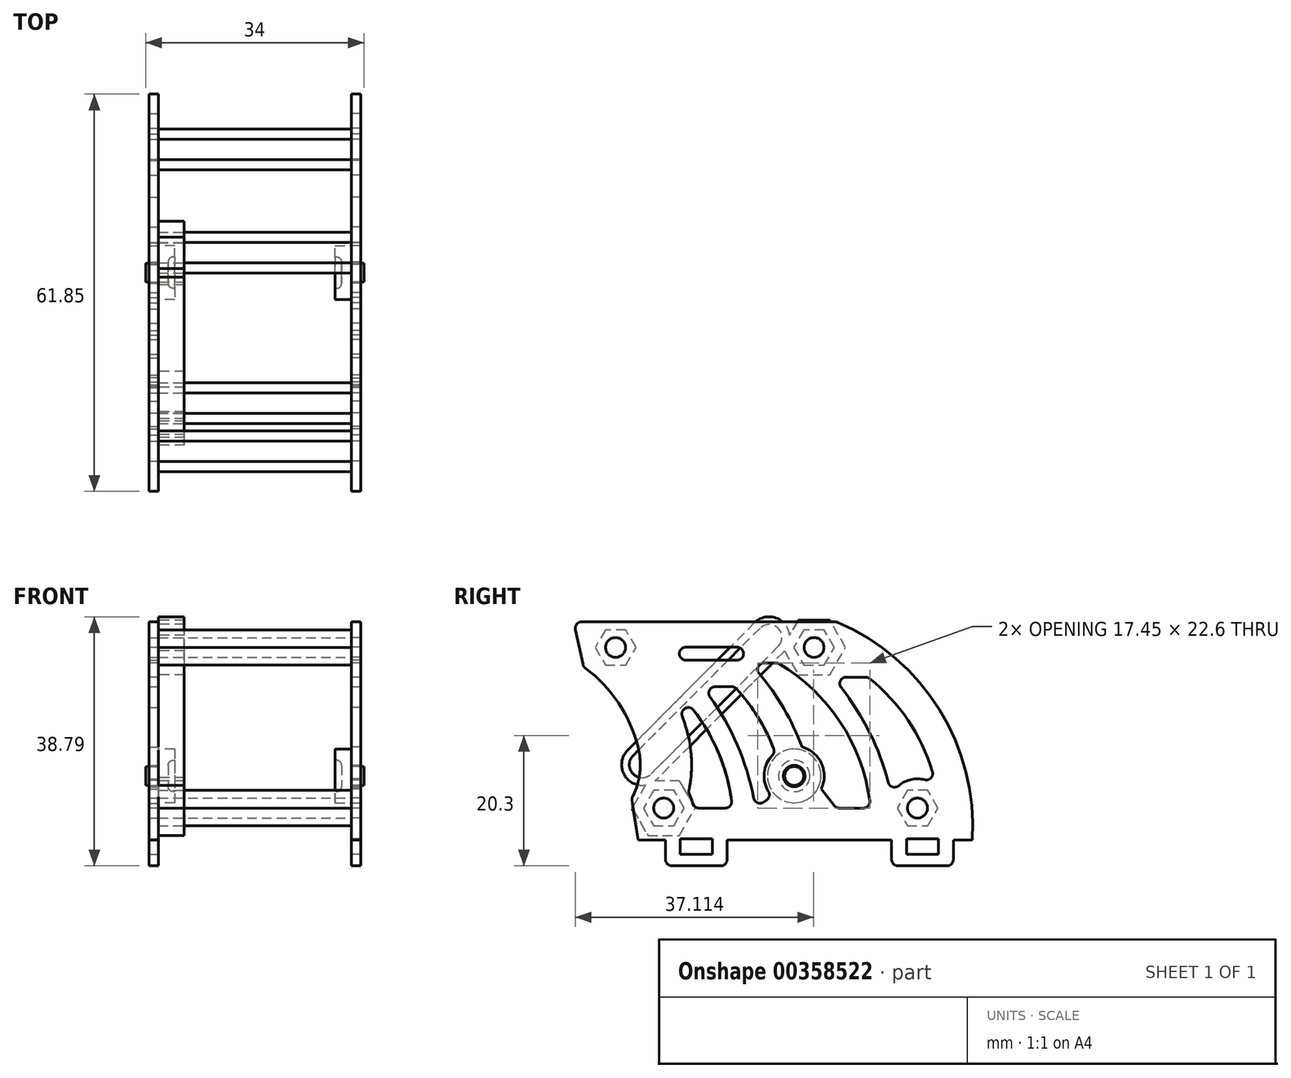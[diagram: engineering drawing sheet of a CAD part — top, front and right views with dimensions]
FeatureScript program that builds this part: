
annotation { "Feature Type Name" : "Feature", "Feature Type Description" : "" }
export const myFeature = defineFeature(function(context is Context, id is Id, definition is map)
    precondition{}
    {
        {
            var Q0;
            Q0=qCreatedBy(makeId("Right.planeOp"),FACE);
            var sketch = newSketch(context, id + "F0", { "sketchPlane" : qUnion([Q0])});
            skLineSegment(sketch, "E0", {"start": v(25.14, 14) * mm, "end": v(22.19, 14) * mm});
            skLineSegment(sketch, "E1.0", {"start": v(-21.61, 10) * mm, "end": v(-14.01, 10) * mm});
            skLineSegment(sketch, "E2", {"start": v(-13.01, 14) * mm, "end": v(-13.01, 11) * mm});
            skLineSegment(sketch, "E3", {"start": v(-22.61, 11) * mm, "end": v(-22.61, 14) * mm});
            skLineSegment(sketch, "E4", {"start": v(-26.89, 14) * mm, "end": v(-27.89, 20.5) * mm});
            skLineSegment(sketch, "E5", {"start": v(-22.61, 14) * mm, "end": v(-26.89, 14) * mm});
            skLineSegment(sketch, "E6", {"start": v(-36.89, 48) * mm, "end": v(3.93, 48) * mm});
            skCircle(sketch, "E7", {"center": v(16.61, 19) * mm, "radius": 1.55 * mm});
            skCircle(sketch, "E8", {"center": v(-22.89, 19) * mm, "radius": 1.55 * mm});
            skCircle(sketch, "E9", {"center": v(-2.58, 24) * mm, "radius": 1.68 * mm});
            skArc(sketch, "E10", {"start": v(25.14, 14) * mm, "mid": v(19.98, 34.4) * mm, "end": v(3.93, 48) * mm});
            skCircle(sketch, "E11", {"center": v(0.51, 44) * mm, "radius": 1.55 * mm});
            skLineSegment(sketch, "E12", {"start": v(-35.39, 41) * mm, "end": v(-36.89, 48) * mm});
            skPoint(sketch, "E13.visualSharp", {"position": v(-22.61, 10) * mm});
            skArc(sketch, "E13.filletArc", {"start": v(-22.61, 11) * mm, "mid": v(-22.32, 10.3) * mm, "end": v(-21.61, 10) * mm});
            skPoint(sketch, "E14.visualSharp", {"position": v(-13.01, 10) * mm});
            skArc(sketch, "E14.filletArc", {"start": v(-14.01, 10) * mm, "mid": v(-13.3, 10.3) * mm, "end": v(-13.01, 11) * mm});
            skLineSegment(sketch, "E15", {"start": v(-20.31, 14.2) * mm, "end": v(-20.31, 11.8) * mm});
            skLineSegment(sketch, "E16", {"start": v(-20.31, 11.8) * mm, "end": v(-15.31, 11.8) * mm});
            skLineSegment(sketch, "E17", {"start": v(-15.31, 11.8) * mm, "end": v(-15.31, 14.2) * mm});
            skLineSegment(sketch, "E18", {"start": v(-15.31, 14.2) * mm, "end": v(-20.31, 14.2) * mm});
            skLineSegment(sketch, "E19.MirrorCS", {"start": v(19.89, 14.2) * mm, "end": v(19.89, 11.8) * mm});
            skLineSegment(sketch, "E20.MirrorCS", {"start": v(14.89, 11.8) * mm, "end": v(14.89, 14.2) * mm});
            skLineSegment(sketch, "E21.MirrorCS", {"start": v(12.59, 14) * mm, "end": v(12.59, 11) * mm});
            skArc(sketch, "E22.MirrorCS", {"start": v(13.59, 10) * mm, "mid": v(12.88, 10.3) * mm, "end": v(12.59, 11) * mm});
            skArc(sketch, "E23.MirrorCS", {"start": v(22.19, 11) * mm, "mid": v(21.9, 10.3) * mm, "end": v(21.19, 10) * mm});
            skPoint(sketch, "E24.MirrorP", {"position": v(23.55, 8) * mm});
            skLineSegment(sketch, "E25.MirrorCS", {"start": v(21.19, 10) * mm, "end": v(13.59, 10) * mm});
            skLineSegment(sketch, "E26.MirrorCS", {"start": v(19.89, 11.8) * mm, "end": v(14.89, 11.8) * mm});
            skLineSegment(sketch, "E27.MirrorCS", {"start": v(14.89, 14.2) * mm, "end": v(19.89, 14.2) * mm});
            skLineSegment(sketch, "E28.MirrorCS", {"start": v(22.19, 11) * mm, "end": v(22.19, 14) * mm});
            skPoint(sketch, "E29.MirrorP", {"position": v(11.75, 8) * mm});
            skArc(sketch, "E30", {"start": v(-27.89, 20.5) * mm, "mid": v(-26.63, 24.4) * mm, "end": v(-26.89, 28.5) * mm});
            skArc(sketch, "E31", {"start": v(-26.89, 28.5) * mm, "mid": v(-30.03, 35.5) * mm, "end": v(-35.39, 41) * mm});
            skLineSegment(sketch, "E32.trimOffspring", {"start": v(12.59, 14) * mm, "end": v(-13.01, 14) * mm});
            skArc(sketch, "E33.0", {"start": v(19.5, 22.5) * mm, "mid": v(15.66, 31.87) * mm, "end": v(8.88, 39.38) * mm});
            skArc(sketch, "E34.0", {"start": v(-18.34, 19) * mm, "mid": v(-18.52, 20.27) * mm, "end": v(-19.04, 21.44) * mm});
            skArc(sketch, "E35.0", {"start": v(19.5, 22.5) * mm, "mid": v(15.65, 23.45) * mm, "end": v(12.53, 21) * mm});
            skArc(sketch, "E36", {"start": v(12.53, 21) * mm, "mid": v(9.15, 30.79) * mm, "end": v(3.38, 39.38) * mm});
            skArc(sketch, "E37.1.0.1", {"start": v(9.32, 19) * mm, "mid": v(4.8, 32.04) * mm, "end": v(-5.15, 41.6) * mm});
            skArc(sketch, "E37.2.0.0", {"start": v(-8.62, 19) * mm, "mid": v(-11.51, 29) * mm, "end": v(-16.89, 37.9) * mm});
            skArc(sketch, "E37.3.0.1", {"start": v(-12.18, 19) * mm, "mid": v(-15.46, 29.9) * mm, "end": v(-22.62, 38.77) * mm});
            skLineSegment(sketch, "E37.direction1", {"start": v(-26.66, 12.96) * mm, "end": v(-37.4, 12.96) * mm, "construction": true});
            skLineSegment(sketch, "E38.trimOffspring", {"start": v(-9.49, 41.6) * mm, "end": v(-5.15, 41.6) * mm});
            skPoint(sketch, "E39.orphan", {"position": v(5.6, 41.6) * mm});
            skPoint(sketch, "E40.orphan", {"position": v(12.88, 19) * mm});
            skArc(sketch, "E41.trimOffspring", {"start": v(-5.54, 27.62) * mm, "mid": v(-8.18, 33.09) * mm, "end": v(-11.89, 37.9) * mm});
            skLineSegment(sketch, "E42.trimOffspring", {"start": v(-8.62, 19) * mm, "end": v(-6.04, 20.85) * mm});
            skPoint(sketch, "E43.orphan", {"position": v(-30.99, 41.6) * mm});
            skLineSegment(sketch, "E44.trimOffspring", {"start": v(-18.34, 19) * mm, "end": v(-12.18, 19) * mm});
            skPoint(sketch, "E45.orphan", {"position": v(20.07, 19) * mm});
            skLineSegment(sketch, "E46", {"start": v(3.96, 19) * mm, "end": v(9.32, 19) * mm});
            skArc(sketch, "E47.trimOffspring", {"start": v(-1.33, 28.5) * mm, "mid": v(-4.77, 35.45) * mm, "end": v(-9.49, 41.6) * mm});
            skCircle(sketch, "E48", {"center": v(-30.39, 44) * mm, "radius": 1.55 * mm});
            skPoint(sketch, "E49.orphan", {"position": v(-26.65, 41.6) * mm});
            skLineSegment(sketch, "E50", {"start": v(-16.89, 37.9) * mm, "end": v(-11.89, 37.9) * mm});
            skLineSegment(sketch, "E51.bottom", {"start": v(-11.57, 42.04) * mm, "end": v(-19.57, 42.04) * mm});
            skLineSegment(sketch, "E51.top", {"start": v(-11.46, 44.04) * mm, "end": v(-19.46, 44.04) * mm});
            skPoint(sketch, "E51.middle", {"position": v(-15.52, 43.04) * mm});
            skArc(sketch, "E52", {"start": v(-19.46, 44.04) * mm, "mid": v(-20.46, 43.1) * mm, "end": v(-19.57, 42.04) * mm});
            skArc(sketch, "E53", {"start": v(-11.57, 42.04) * mm, "mid": v(-10.46, 42.98) * mm, "end": v(-11.46, 44.04) * mm});
            skArc(sketch, "E54.0", {"start": v(-19.13, 30.47) * mm, "mid": v(-20.56, 34.75) * mm, "end": v(-22.62, 38.77) * mm});
            skArc(sketch, "E54.1", {"start": v(-19.04, 21.44) * mm, "mid": v(-18.54, 25.96) * mm, "end": v(-19.13, 30.47) * mm});
            skLineSegment(sketch, "E55", {"start": v(3.38, 39.38) * mm, "end": v(8.88, 39.38) * mm});
            skLineSegment(sketch, "E56", {"start": v(-2.58, 24) * mm, "end": v(-2.58, 30.46) * mm, "construction": true});
            skArc(sketch, "E57", {"start": v(1.64, 21.98) * mm, "mid": v(1.67, 25.94) * mm, "end": v(-1.33, 28.5) * mm});
            skPoint(sketch, "E58.start.orphan", {"position": v(-4.86, 25.5) * mm});
            skLineSegment(sketch, "E59", {"start": v(1.64, 21.98) * mm, "end": v(3.96, 19) * mm});
            skArc(sketch, "E60.trimOffspring", {"start": v(-5.54, 27.62) * mm, "mid": v(-7.24, 24.34) * mm, "end": v(-6.04, 20.85) * mm});
            skLineSegment(sketch, "E61", {"start": v(17.39, 14.2) * mm, "end": v(17.39, 10) * mm, "construction": true});
            skSolve(sketch);
        }
        {
            var Q0;
            Q0=qSketchRegion(id+"F0",true);
            extrude(context, id + "F1", {"entities" : qUnion([Q0]), "depth" : 1.5 * mm});
        }
        {
            var Q0;
            Q0=makeQuery(id+"F1.opExtrude","SWEPT_EDGE",EDGE,{"disambiguationData":[OSD([sQuery(id+"F0.wireOp",EDGE,"E6"),sQuery(id+"F0.wireOp",EDGE,"E12")])]});
            var Q1;
            Q1=makeQuery(id+"F1.opExtrude","SWEPT_EDGE",EDGE,{"disambiguationData":[OSD([sQuery(id+"F0.wireOp",EDGE,"E12"),sQuery(id+"F0.wireOp",EDGE,"E31")])]});
            var Q2;
            Q2=makeQuery(id+"F1.opExtrude","SWEPT_EDGE",EDGE,{"disambiguationData":[OSD([sQuery(id+"F0.wireOp",EDGE,"E4"),sQuery(id+"F0.wireOp",EDGE,"E30")])]});
            var Q3;
            Q3=makeQuery(id+"F1.opExtrude","SWEPT_EDGE",EDGE,{"disambiguationData":[OSD([sQuery(id+"F0.wireOp",EDGE,"E6"),sQuery(id+"F0.wireOp",EDGE,"E10")])]});
            var Q4;
            Q4=makeQuery(id+"F1.opExtrude","SWEPT_EDGE",EDGE,{"disambiguationData":[OSD([sQuery(id+"F0.wireOp",EDGE,"E37.3.0.1"),sQuery(id+"F0.wireOp",EDGE,"E44.trimOffspring")])]});
            var Q5;
            Q5=makeQuery(id+"F1.opExtrude","SWEPT_EDGE",EDGE,{"disambiguationData":[OSD([sQuery(id+"F0.wireOp",EDGE,"E34.0"),sQuery(id+"F0.wireOp",EDGE,"E44.trimOffspring")])]});
            var Q6;
            Q6=makeQuery(id+"F1.opExtrude","SWEPT_EDGE",EDGE,{"disambiguationData":[OSD([sQuery(id+"F0.wireOp",EDGE,"E34.0"),sQuery(id+"F0.wireOp",EDGE,"8874c545-3156-4a57-8101-8b2921fbed11.trimOffspring")])]});
            var Q7;
            Q7=makeQuery(id+"F1.opExtrude","SWEPT_EDGE",EDGE,{"disambiguationData":[OSD([sQuery(id+"F0.wireOp",EDGE,"E37.2.0.0"),sQuery(id+"F0.wireOp",EDGE,"E42.trimOffspring")])]});
            var Q8;
            Q8=makeQuery(id+"F1.opExtrude","SWEPT_EDGE",EDGE,{"disambiguationData":[OSD([sQuery(id+"F0.wireOp",EDGE,"E42.trimOffspring"),sQuery(id+"F0.wireOp",EDGE,"E58")])]});
            var Q9;
            Q9=makeQuery(id+"F1.opExtrude","SWEPT_EDGE",EDGE,{"disambiguationData":[OSD([sQuery(id+"F0.wireOp",EDGE,"E41.trimOffspring"),sQuery(id+"F0.wireOp",EDGE,"E58")])]});
            var Q10;
            Q10=makeQuery(id+"F1.opExtrude","SWEPT_EDGE",EDGE,{"disambiguationData":[OSD([sQuery(id+"F0.wireOp",EDGE,"73401603-de56-4370-a730-08e3040fd849.1"),sQuery(id+"F0.wireOp",EDGE,"Jx6L4jmH-5SSZ-aaiZ-kghy-jZzfS1jKpH57")])]});
            var Q11;
            Q11=makeQuery(id+"F1.opExtrude","SWEPT_EDGE",EDGE,{"disambiguationData":[OSD([sQuery(id+"F0.wireOp",EDGE,"E37.3.0.1"),sQuery(id+"F0.wireOp",EDGE,"Jx6L4jmH-5SSZ-aaiZ-kghy-jZzfS1jKpH57")])]});
            var Q12;
            Q12=makeQuery(id+"F1.opExtrude","SWEPT_EDGE",EDGE,{"disambiguationData":[OSD([sQuery(id+"F0.wireOp",EDGE,"E37.2.0.0"),sQuery(id+"F0.wireOp",EDGE,"42fc0774-851a-4965-af8c-24a0156e8afa.trimOffspring")])]});
            var Q13;
            Q13=makeQuery(id+"F1.opExtrude","SWEPT_EDGE",EDGE,{"disambiguationData":[OSD([sQuery(id+"F0.wireOp",EDGE,"E38.trimOffspring"),sQuery(id+"F0.wireOp",EDGE,"E47.trimOffspring")])]});
            var Q14;
            Q14=makeQuery(id+"F1.opExtrude","SWEPT_EDGE",EDGE,{"disambiguationData":[OSD([sQuery(id+"F0.wireOp",EDGE,"4fd4c681-5e1e-4616-ba06-4993dd0134da.0"),sQuery(id+"F0.wireOp",EDGE,"E36")])]});
            var Q15;
            Q15=makeQuery(id+"F1.opExtrude","SWEPT_EDGE",EDGE,{"disambiguationData":[OSD([sQuery(id+"F0.wireOp",EDGE,"E37.1.0.1"),sQuery(id+"F0.wireOp",EDGE,"E38.trimOffspring")])]});
            var Q16;
            Q16=makeQuery(id+"F1.opExtrude","SWEPT_EDGE",EDGE,{"disambiguationData":[OSD([sQuery(id+"F0.wireOp",EDGE,"E33.0"),sQuery(id+"F0.wireOp",EDGE,"4fd4c681-5e1e-4616-ba06-4993dd0134da.0")])]});
            var Q17;
            Q17=makeQuery(id+"F1.opExtrude","SWEPT_EDGE",EDGE,{"disambiguationData":[OSD([sQuery(id+"F0.wireOp",EDGE,"E33.0"),sQuery(id+"F0.wireOp",EDGE,"E35.0")])]});
            var Q18;
            Q18=makeQuery(id+"F1.opExtrude","SWEPT_EDGE",EDGE,{"disambiguationData":[OSD([sQuery(id+"F0.wireOp",EDGE,"E35.0"),sQuery(id+"F0.wireOp",EDGE,"E36")])]});
            var Q19;
            Q19=makeQuery(id+"F1.opExtrude","SWEPT_EDGE",EDGE,{"disambiguationData":[OSD([sQuery(id+"F0.wireOp",EDGE,"E37.1.0.1"),sQuery(id+"F0.wireOp",EDGE,"E46")])]});
            var Q20;
            Q20=makeQuery(id+"F1.opExtrude","SWEPT_EDGE",EDGE,{"disambiguationData":[OSD([sQuery(id+"F0.wireOp",EDGE,"E37.1.0.0"),sQuery(id+"F0.wireOp",EDGE,"E46")])]});
            var Q21;
            Q21=makeQuery(id+"F1.opExtrude","SWEPT_EDGE",EDGE,{"disambiguationData":[OSD([sQuery(id+"F0.wireOp",EDGE,"42fc0774-851a-4965-af8c-24a0156e8afa.trimOffspring"),sQuery(id+"F0.wireOp",EDGE,"E41.trimOffspring")])]});
            fillet(context, id + "F2", {"entities" : qUnion([Q0, Q1, Q2, Q3, Q4, Q5, Q6, Q7, Q8, Q9, Q10, Q11, Q12, Q13, Q14, Q15, Q16, Q17, Q18, Q19, Q20, Q21]), "radius" : 1 * mm, "tangentPropagation" : true, "allowEdgeOverflow" : false});
        }
        {
            var Q0;
            Q0=makeQuery(id+"F1.opExtrude","CAP_FACE",FACE,{"disambiguationData":[OSD([sQuery(id+"F0.wireOp",EDGE,"HIeokZtu-qvy5-WvQW-1yrS-XgbBhr9NXsEF"),sQuery(id+"F0.wireOp",EDGE,"ndsYfQKX-n3Rt-GvvT-uKDq-gzqfGxigb06w"),sQuery(id+"F0.wireOp",EDGE,"1NnFIVhj-AYXC-JC9t-m1gl-o3tyJmiQpsGb"),sQuery(id+"F0.wireOp",EDGE,"E0"),sQuery(id+"F0.wireOp",EDGE,"E1.0"),sQuery(id+"F0.wireOp",EDGE,"E2"),sQuery(id+"F0.wireOp",EDGE,"E3"),sQuery(id+"F0.wireOp",EDGE,"xJjsbCEC-m1Jw-8FaK-kHz9-E4O4SPVdDl4v"),sQuery(id+"F0.wireOp",EDGE,"E4"),sQuery(id+"F0.wireOp",EDGE,"E5"),sQuery(id+"F0.wireOp",EDGE,"E6"),sQuery(id+"F0.wireOp",EDGE,"QagRSCTP-biDV-1D91-L336-It3P8s5A26IG"),sQuery(id+"F0.wireOp",EDGE,"E7"),sQuery(id+"F0.wireOp",EDGE,"E8")])],"isStart":true});
            var sketch = newSketch(context, id + "F3", { "sketchPlane" : qUnion([Q0])});
            skCircle(sketch, "E62.cCircle", {"center": v(-16.61, 19) * mm, "radius": 2.75 * mm, "construction": true});
            skLineSegment(sketch, "E62.0", {"start": v(-18.2, 21.75) * mm, "end": v(-15.03, 21.75) * mm});
            skLineSegment(sketch, "E62.1", {"start": v(-15.03, 21.75) * mm, "end": v(-13.44, 19) * mm});
            skLineSegment(sketch, "E62.2", {"start": v(-13.44, 19) * mm, "end": v(-15.03, 16.25) * mm});
            skLineSegment(sketch, "E62.3", {"start": v(-15.03, 16.25) * mm, "end": v(-18.2, 16.25) * mm});
            skLineSegment(sketch, "E62.4", {"start": v(-18.2, 16.25) * mm, "end": v(-19.79, 19) * mm});
            skLineSegment(sketch, "E62.5", {"start": v(-19.79, 19) * mm, "end": v(-18.2, 21.75) * mm});
            skPoint(sketch, "E62.0.midPoint", {"position": v(-16.61, 21.75) * mm});
            skCircle(sketch, "E63.cCircle", {"center": v(22.89, 19) * mm, "radius": 2.75 * mm, "construction": true});
            skLineSegment(sketch, "E63.0", {"start": v(21.3, 21.75) * mm, "end": v(24.47, 21.75) * mm});
            skLineSegment(sketch, "E63.1", {"start": v(24.47, 21.75) * mm, "end": v(26.06, 19) * mm});
            skLineSegment(sketch, "E63.2", {"start": v(26.06, 19) * mm, "end": v(24.47, 16.25) * mm});
            skLineSegment(sketch, "E63.3", {"start": v(24.47, 16.25) * mm, "end": v(21.3, 16.25) * mm});
            skLineSegment(sketch, "E63.4", {"start": v(21.3, 16.25) * mm, "end": v(19.71, 19) * mm});
            skLineSegment(sketch, "E63.5", {"start": v(19.71, 19) * mm, "end": v(21.3, 21.75) * mm});
            skPoint(sketch, "E63.0.midPoint", {"position": v(22.89, 21.75) * mm});
            skCircle(sketch, "E64.cCircle", {"center": v(-0.51, 44) * mm, "radius": 2.75 * mm, "construction": true});
            skLineSegment(sketch, "E64.0", {"start": v(-2.1, 46.75) * mm, "end": v(1.08, 46.75) * mm});
            skLineSegment(sketch, "E64.1", {"start": v(1.08, 46.75) * mm, "end": v(2.66, 44) * mm});
            skLineSegment(sketch, "E64.2", {"start": v(2.66, 44) * mm, "end": v(1.08, 41.25) * mm});
            skLineSegment(sketch, "E64.3", {"start": v(1.08, 41.25) * mm, "end": v(-2.1, 41.25) * mm});
            skLineSegment(sketch, "E64.4", {"start": v(-2.1, 41.25) * mm, "end": v(-3.69, 44) * mm});
            skLineSegment(sketch, "E64.5", {"start": v(-3.69, 44) * mm, "end": v(-2.1, 46.75) * mm});
            skPoint(sketch, "E64.0.midPoint", {"position": v(-0.51, 46.75) * mm});
            skCircle(sketch, "E65.cCircle", {"center": v(30.39, 44) * mm, "radius": 2.75 * mm, "construction": true});
            skLineSegment(sketch, "E65.0", {"start": v(31.97, 46.75) * mm, "end": v(33.56, 44) * mm});
            skLineSegment(sketch, "E65.1", {"start": v(33.56, 44) * mm, "end": v(31.97, 41.25) * mm});
            skLineSegment(sketch, "E65.2", {"start": v(31.97, 41.25) * mm, "end": v(28.8, 41.25) * mm});
            skLineSegment(sketch, "E65.3", {"start": v(28.8, 41.25) * mm, "end": v(27.21, 44) * mm});
            skLineSegment(sketch, "E65.4", {"start": v(27.21, 44) * mm, "end": v(28.8, 46.75) * mm});
            skLineSegment(sketch, "E65.5", {"start": v(28.8, 46.75) * mm, "end": v(31.97, 46.75) * mm});
            skPoint(sketch, "E65.0.midPoint", {"position": v(32.77, 45.38) * mm});
            skSolve(sketch);
        }
        {
            var Q0;
            Q0=makeQuery(id+"F3.imprint","IMPRINT",FACE,{"disambiguationData":[TD([[makeQuery(id+"F3.imprint","IMPRINT",EDGE,{"derivedFrom":sQuery(id+"F3.wireOp",EDGE,"E62.0")}),-1.0]])]});
            var Q1;
            Q1=makeQuery(id+"F3.imprint","IMPRINT",FACE,{"disambiguationData":[TD([[makeQuery(id+"F3.imprint","IMPRINT",EDGE,{"derivedFrom":sQuery(id+"F3.wireOp",EDGE,"E63.0")}),-1.0]])]});
            var Q2;
            Q2=makeQuery(id+"F3.imprint","IMPRINT",FACE,{"disambiguationData":[TD([[makeQuery(id+"F3.imprint","IMPRINT",EDGE,{"derivedFrom":sQuery(id+"F3.wireOp",EDGE,"E64.0")}),-1.0]])]});
            var Q3;
            Q3=makeQuery(id+"F3.imprint","IMPRINT",FACE,{"disambiguationData":[TD([[makeQuery(id+"F3.imprint","IMPRINT",EDGE,{"derivedFrom":sQuery(id+"F3.wireOp",EDGE,"E65.0")}),-1.0]])]});
            extrude(context, id + "F4", {"entities" : qUnion([Q0, Q1, Q2, Q3]), "depth" : 30 * mm});
        }
        {
            var Q0;
            Q0=makeQuery(id+"F1.opExtrude","CAP_FACE",FACE,{"disambiguationData":[OSD([sQuery(id+"F0.wireOp",EDGE,"E0"),sQuery(id+"F0.wireOp",EDGE,"E1.0"),sQuery(id+"F0.wireOp",EDGE,"E2"),sQuery(id+"F0.wireOp",EDGE,"E3"),sQuery(id+"F0.wireOp",EDGE,"E4"),sQuery(id+"F0.wireOp",EDGE,"E5"),sQuery(id+"F0.wireOp",EDGE,"E6"),sQuery(id+"F0.wireOp",EDGE,"E7"),sQuery(id+"F0.wireOp",EDGE,"E8"),sQuery(id+"F0.wireOp",EDGE,"E9"),sQuery(id+"F0.wireOp",EDGE,"E10"),sQuery(id+"F0.wireOp",EDGE,"E11"),sQuery(id+"F0.wireOp",EDGE,"E12"),sQuery(id+"F0.wireOp",EDGE,"E13.filletArc"),sQuery(id+"F0.wireOp",EDGE,"E14.filletArc"),sQuery(id+"F0.wireOp",EDGE,"E15"),sQuery(id+"F0.wireOp",EDGE,"E16"),sQuery(id+"F0.wireOp",EDGE,"E17"),sQuery(id+"F0.wireOp",EDGE,"E18"),sQuery(id+"F0.wireOp",EDGE,"E19.MirrorCS"),sQuery(id+"F0.wireOp",EDGE,"E20.MirrorCS"),sQuery(id+"F0.wireOp",EDGE,"E21.MirrorCS"),sQuery(id+"F0.wireOp",EDGE,"E22.MirrorCS"),sQuery(id+"F0.wireOp",EDGE,"E23.MirrorCS"),sQuery(id+"F0.wireOp",EDGE,"E25.MirrorCS"),sQuery(id+"F0.wireOp",EDGE,"E26.MirrorCS"),sQuery(id+"F0.wireOp",EDGE,"E27.MirrorCS"),sQuery(id+"F0.wireOp",EDGE,"E28.MirrorCS"),sQuery(id+"F0.wireOp",EDGE,"E30"),sQuery(id+"F0.wireOp",EDGE,"E31"),sQuery(id+"F0.wireOp",EDGE,"E32.trimOffspring"),sQuery(id+"F0.wireOp",EDGE,"E33.0"),sQuery(id+"F0.wireOp",EDGE,"73401603-de56-4370-a730-08e3040fd849.1"),sQuery(id+"F0.wireOp",EDGE,"4fd4c681-5e1e-4616-ba06-4993dd0134da.0"),sQuery(id+"F0.wireOp",EDGE,"E34.0"),sQuery(id+"F0.wireOp",EDGE,"E35.0"),sQuery(id+"F0.wireOp",EDGE,"E36"),sQuery(id+"F0.wireOp",EDGE,"E37.1.0.0"),sQuery(id+"F0.wireOp",EDGE,"E37.1.0.1"),sQuery(id+"F0.wireOp",EDGE,"E37.2.0.0"),sQuery(id+"F0.wireOp",EDGE,"E37.3.0.1"),sQuery(id+"F0.wireOp",EDGE,"E38.trimOffspring"),sQuery(id+"F0.wireOp",EDGE,"E41.trimOffspring"),sQuery(id+"F0.wireOp",EDGE,"E42.trimOffspring"),sQuery(id+"F0.wireOp",EDGE,"8874c545-3156-4a57-8101-8b2921fbed11.trimOffspring"),sQuery(id+"F0.wireOp",EDGE,"E44.trimOffspring"),sQuery(id+"F0.wireOp",EDGE,"E46"),sQuery(id+"F0.wireOp",EDGE,"E58"),sQuery(id+"F0.wireOp",EDGE,"E47.trimOffspring"),sQuery(id+"F0.wireOp",EDGE,"bd3d0f78-ffc8-42c1-8f79-e99b2f7a1da2.trimOffspring"),sQuery(id+"F0.wireOp",EDGE,"E48"),sQuery(id+"F0.wireOp",EDGE,"Jx6L4jmH-5SSZ-aaiZ-kghy-jZzfS1jKpH57"),sQuery(id+"F0.wireOp",EDGE,"E50"),sQuery(id+"F0.wireOp",EDGE,"E51.bottom"),sQuery(id+"F0.wireOp",EDGE,"E51.top"),sQuery(id+"F0.wireOp",EDGE,"E52"),sQuery(id+"F0.wireOp",EDGE,"E53")])],"isStart":true});
            var sketch = newSketch(context, id + "F5", { "sketchPlane" : qUnion([Q0])});
            skCircle(sketch, "E66.0", {"center": v(2.58, 24) * mm, "radius": 1.47 * mm});
            skCircle(sketch, "E67.0", {"center": v(2.58, 24) * mm, "radius": 4.17 * mm});
            skSolve(sketch);
        }
        {
            var Q0;
            Q0=makeQuery(id+"F5.imprint","IMPRINT",FACE,{"disambiguationData":[TD([[makeQuery(id+"F5.imprint","IMPRINT",EDGE,{"derivedFrom":sQuery(id+"F5.wireOp",EDGE,"E66.0")}),1.0]])]});
            extrude(context, id + "F6", {"entities" : qUnion([Q0]), "oppositeDirection" : true, "depth" : 2 * mm});
        }
        {
            var Q0;
            Q0=makeQuery(id+"F5.imprint","IMPRINT",FACE,{"disambiguationData":[TD([[makeQuery(id+"F5.imprint","IMPRINT",EDGE,{"derivedFrom":sQuery(id+"F5.wireOp",EDGE,"E66.0")}),1.0]])]});
            var Q1;
            Q1=makeQuery(id+"F5.imprint","IMPRINT",FACE,{"disambiguationData":[TD([[makeQuery(id+"F5.imprint","IMPRINT",EDGE,{"derivedFrom":sQuery(id+"F5.wireOp",EDGE,"E66.0")}),-1.0]])]});
            var Q2;
            Q2=makeQuery(id+"F5.imprint","IMPRINT",FACE,{"disambiguationData":[TD([[makeQuery(id+"F5.imprint","IMPRINT",EDGE,{"derivedFrom":sQuery(id+"F5.wireOp",EDGE,"aw567Un7-uZuC-Ed0T-qZZ2-tGJGIrZdYuvX")}),1.0]])]});
            var Q3;
            Q3=makeQuery(id+"F5.imprint","IMPRINT",FACE,{"disambiguationData":[TD([[makeQuery(id+"F5.imprint","IMPRINT",EDGE,{"derivedFrom":sQuery(id+"F5.wireOp",EDGE,"E67.0")}),1.0]])]});
            extrude(context, id + "F7", {"entities" : qUnion([Q0, Q1, Q2, Q3]), "operationType" : NewBodyOperationType.ADD, "depth" : 2.5 * mm});
        }
        {
            var Q0;
            Q0=makeQuery(id+"F7.opExtrude","CAP_FACE",FACE,{"disambiguationData":[OSD([sQuery(id+"F5.wireOp",EDGE,"E67.0")])],"isStart":false});
            var sketch = newSketch(context, id + "F8", { "sketchPlane" : qUnion([Q0])});
            skCircle(sketch, "E68", {"center": v(2.58, 24) * mm, "radius": 2.45 * mm});
            skSolve(sketch);
        }
        {
            var Q0;
            Q0=qSketchRegion(id+"F8",true);
            extrude(context, id + "F9", {"entities" : qUnion([Q0]), "operationType" : NewBodyOperationType.REMOVE, "oppositeDirection" : true, "depth" : 1 * mm});
        }
        {
            var Q0;
            Q0=makeQuery(id+"F9.boolean.opBoolean","COPY",EDGE,{"derivedFrom":makeQuery(id+"F9.opExtrude","CAP_EDGE",EDGE,{"disambiguationData":[OSD([sQuery(id+"F8.wireOp",EDGE,"E68")])],"isStart":false})});
            var Q1;
            Q1=makeQuery(id+"F6.opExtrude","CAP_EDGE",EDGE,{"disambiguationData":[OSD([sQuery(id+"F5.wireOp",EDGE,"E66.0")])],"isStart":true});
            fillet(context, id + "F10", {"entities" : qUnion([Q0, Q1]), "radius" : .8 * mm, "tangentPropagation" : true, "allowEdgeOverflow" : false});
        }
        {
            var Q0;
            Q0=makeQuery(id+"F4.opExtrude","CAP_FACE",FACE,{"disambiguationData":[OSD([sQuery(id+"F0.wireOp",EDGE,"E48"),sQuery(id+"F3.wireOp",EDGE,"E65.0"),sQuery(id+"F3.wireOp",EDGE,"E65.1"),sQuery(id+"F3.wireOp",EDGE,"E65.2"),sQuery(id+"F3.wireOp",EDGE,"E65.3"),sQuery(id+"F3.wireOp",EDGE,"E65.4"),sQuery(id+"F3.wireOp",EDGE,"E65.5")])],"isStart":true});
            var Q1;
            Q1=makeQuery(id+"F4.opExtrude","CAP_FACE",FACE,{"disambiguationData":[OSD([sQuery(id+"F0.wireOp",EDGE,"E48"),sQuery(id+"F3.wireOp",EDGE,"E65.0"),sQuery(id+"F3.wireOp",EDGE,"E65.1"),sQuery(id+"F3.wireOp",EDGE,"E65.2"),sQuery(id+"F3.wireOp",EDGE,"E65.3"),sQuery(id+"F3.wireOp",EDGE,"E65.4"),sQuery(id+"F3.wireOp",EDGE,"E65.5")])],"isStart":false});
            cPlane(context, id + "F11", {"entities" : qUnion([Q0, Q1]), "cplaneType" : CPlaneType.MID_PLANE, "offset" : 25 * mm, "width" : 150 * mm, "height" : 150 * mm});
        }
        {
            var Q0;
            Q0=makeQuery(id+"F1.opExtrude","SWEPT_BODY",BODY,{"disambiguationData":[OSD([sQuery(id+"F0.wireOp",EDGE,"HIeokZtu-qvy5-WvQW-1yrS-XgbBhr9NXsEF"),sQuery(id+"F0.wireOp",EDGE,"ndsYfQKX-n3Rt-GvvT-uKDq-gzqfGxigb06w"),sQuery(id+"F0.wireOp",EDGE,"1NnFIVhj-AYXC-JC9t-m1gl-o3tyJmiQpsGb"),sQuery(id+"F0.wireOp",EDGE,"E0"),sQuery(id+"F0.wireOp",EDGE,"E1.0"),sQuery(id+"F0.wireOp",EDGE,"E2"),sQuery(id+"F0.wireOp",EDGE,"E3"),sQuery(id+"F0.wireOp",EDGE,"xJjsbCEC-m1Jw-8FaK-kHz9-E4O4SPVdDl4v"),sQuery(id+"F0.wireOp",EDGE,"E4"),sQuery(id+"F0.wireOp",EDGE,"E5"),sQuery(id+"F0.wireOp",EDGE,"E6"),sQuery(id+"F0.wireOp",EDGE,"QagRSCTP-biDV-1D91-L336-It3P8s5A26IG"),sQuery(id+"F0.wireOp",EDGE,"E7"),sQuery(id+"F0.wireOp",EDGE,"E8"),sQuery(id+"F0.wireOp",EDGE,"E9")])]});
            var Q1;
            Q1=makeQuery(id+"F6.opExtrude","SWEPT_BODY",BODY,{"disambiguationData":[OSD([sQuery(id+"F5.wireOp",EDGE,"E66.0")])]});
            var Q2;
            Q2=qCreatedBy(id+"F11.planeOp",FACE);
            mirror(context, id + "F12", {"entities" : qUnion([Q0, Q1]), "mirrorPlane" : qUnion([Q2])});
        }
        {
            var Q0;
            Q0=makeQuery(id+"F4.opExtrude","CAP_FACE",FACE,{"disambiguationData":[OSD([sQuery(id+"F0.wireOp",EDGE,"E11"),sQuery(id+"F3.wireOp",EDGE,"E64.0"),sQuery(id+"F3.wireOp",EDGE,"E64.1"),sQuery(id+"F3.wireOp",EDGE,"E64.2"),sQuery(id+"F3.wireOp",EDGE,"E64.3"),sQuery(id+"F3.wireOp",EDGE,"E64.4"),sQuery(id+"F3.wireOp",EDGE,"E64.5")])],"isStart":false});
            var sketch = newSketch(context, id + "F13", { "sketchPlane" : qUnion([Q0])});
            skLineSegment(sketch, "E69.0", {"start": v(1.08, 46.75) * mm, "end": v(2.66, 44) * mm});
            skLineSegment(sketch, "E69.1", {"start": v(-2.1, 46.75) * mm, "end": v(1.08, 46.75) * mm});
            skLineSegment(sketch, "E69.2", {"start": v(-3.69, 44) * mm, "end": v(-2.1, 46.75) * mm});
            skLineSegment(sketch, "E69.3", {"start": v(-2.1, 41.25) * mm, "end": v(-3.69, 44) * mm});
            skLineSegment(sketch, "E69.4", {"start": v(1.08, 41.25) * mm, "end": v(-2.1, 41.25) * mm});
            skLineSegment(sketch, "E69.5", {"start": v(2.66, 44) * mm, "end": v(1.08, 41.25) * mm});
            skLineSegment(sketch, "E69.6", {"start": v(24.47, 21.75) * mm, "end": v(26.06, 19) * mm});
            skLineSegment(sketch, "E69.7", {"start": v(21.3, 21.75) * mm, "end": v(24.47, 21.75) * mm});
            skLineSegment(sketch, "E69.8", {"start": v(19.71, 19) * mm, "end": v(21.3, 21.75) * mm});
            skLineSegment(sketch, "E69.9", {"start": v(21.3, 16.25) * mm, "end": v(19.71, 19) * mm});
            skLineSegment(sketch, "E69.10", {"start": v(24.47, 16.25) * mm, "end": v(21.3, 16.25) * mm});
            skLineSegment(sketch, "E69.11", {"start": v(26.06, 19) * mm, "end": v(24.47, 16.25) * mm});
            skLineSegment(sketch, "E70.0", {"start": v(-2.96, 48.25) * mm, "end": v(1.94, 48.25) * mm});
            skLineSegment(sketch, "E70.1", {"start": v(4.4, 44) * mm, "end": v(1.94, 39.75) * mm});
            skLineSegment(sketch, "E70.2", {"start": v(1.94, 39.75) * mm, "end": v(-2.96, 39.75) * mm});
            skLineSegment(sketch, "E70.3", {"start": v(1.94, 48.25) * mm, "end": v(4.4, 44) * mm});
            skLineSegment(sketch, "E70.4", {"start": v(-2.96, 39.75) * mm, "end": v(-5.42, 44) * mm});
            skLineSegment(sketch, "E70.5", {"start": v(-5.42, 44) * mm, "end": v(-2.96, 48.25) * mm});
            skLineSegment(sketch, "E71.0", {"start": v(20.43, 23.25) * mm, "end": v(25.9, 23.25) * mm});
            skLineSegment(sketch, "E71.1", {"start": v(27.8, 19) * mm, "end": v(25.34, 14.75) * mm});
            skLineSegment(sketch, "E71.2", {"start": v(25.34, 14.75) * mm, "end": v(20.43, 14.75) * mm});
            skLineSegment(sketch, "E71.3", {"start": v(24.56, 24.6) * mm, "end": v(27.8, 19) * mm});
            skLineSegment(sketch, "E71.4", {"start": v(20.43, 14.75) * mm, "end": v(17.98, 19) * mm});
            skLineSegment(sketch, "E71.5", {"start": v(17.98, 19) * mm, "end": v(20.43, 23.25) * mm});
            skLineSegment(sketch, "E72.left", {"start": v(5.07, 44.18) * mm, "end": v(24.83, 24.33) * mm});
            skLineSegment(sketch, "E72.right", {"start": v(7.9, 47) * mm, "end": v(27.66, 27.16) * mm});
            skArc(sketch, "E73", {"start": v(7.9, 47) * mm, "mid": v(5.08, 47) * mm, "end": v(5.07, 44.18) * mm});
            skArc(sketch, "E74", {"start": v(24.83, 24.33) * mm, "mid": v(27.65, 24.33) * mm, "end": v(27.66, 27.16) * mm});
            skArc(sketch, "E75.0", {"start": v(8.76, 47.85) * mm, "mid": v(4.23, 47.86) * mm, "end": v(4.22, 43.33) * mm});
            skLineSegment(sketch, "E75.1", {"start": v(8.76, 47.85) * mm, "end": v(28.51, 28) * mm});
            skArc(sketch, "E75.2", {"start": v(23.98, 23.49) * mm, "mid": v(28.5, 23.48) * mm, "end": v(28.51, 28) * mm});
            skLineSegment(sketch, "E75.3", {"start": v(4.22, 43.33) * mm, "end": v(23.98, 23.49) * mm});
            skSolve(sketch);
        }
        {
            var Q0;
            {var subQ0=sQuery(id+"F13.wireOp",EDGE,"E70.3");Q0=makeQuery(id+"F13.imprint","IMPRINT",FACE,{"disambiguationData":[TD([[makeQuery(id+"F13.imprint","IMPRINT",EDGE,{"derivedFrom":subQ0}),-1.0]])]});}
            var Q1;
            Q1=makeQuery(id+"F13.imprint","IMPRINT",FACE,{"disambiguationData":[TD([[makeQuery(id+"F13.imprint","IMPRINT",EDGE,{"derivedFrom":sQuery(id+"F13.wireOp",EDGE,"E69.0")}),1.0]])]});
            var Q2;
            {var subQ6=sQuery(id+"F13.wireOp",EDGE,"E70.3");Q2=makeQuery(id+"F13.imprint","IMPRINT",FACE,{"disambiguationData":[TD([[makeQuery(id+"F13.imprint","IMPRINT",EDGE,{"derivedFrom":subQ6}),1.0]])]});}
            var Q3;
            {var subQ2=sQuery(id+"F13.wireOp",EDGE,"E71.3");Q3=makeQuery(id+"F13.imprint","IMPRINT",FACE,{"disambiguationData":[TD([[makeQuery(id+"F13.imprint","IMPRINT",EDGE,{"derivedFrom":subQ2}),1.0]])]});}
            var Q4;
            Q4=makeQuery(id+"F13.imprint","IMPRINT",FACE,{"disambiguationData":[TD([[makeQuery(id+"F13.imprint","IMPRINT",EDGE,{"derivedFrom":sQuery(id+"F13.wireOp",EDGE,"E69.6")}),1.0]])]});
            var Q5;
            {var subQ0=sQuery(id+"F13.wireOp",EDGE,"E71.3");Q5=makeQuery(id+"F13.imprint","IMPRINT",FACE,{"disambiguationData":[TD([[makeQuery(id+"F13.imprint","IMPRINT",EDGE,{"derivedFrom":subQ0}),-1.0]])]});}
            extrude(context, id + "F14", {"entities" : qUnion([Q0, Q1, Q2, Q3, Q4, Q5]), "oppositeDirection" : true, "depth" : 4 * mm});
        }
    });
